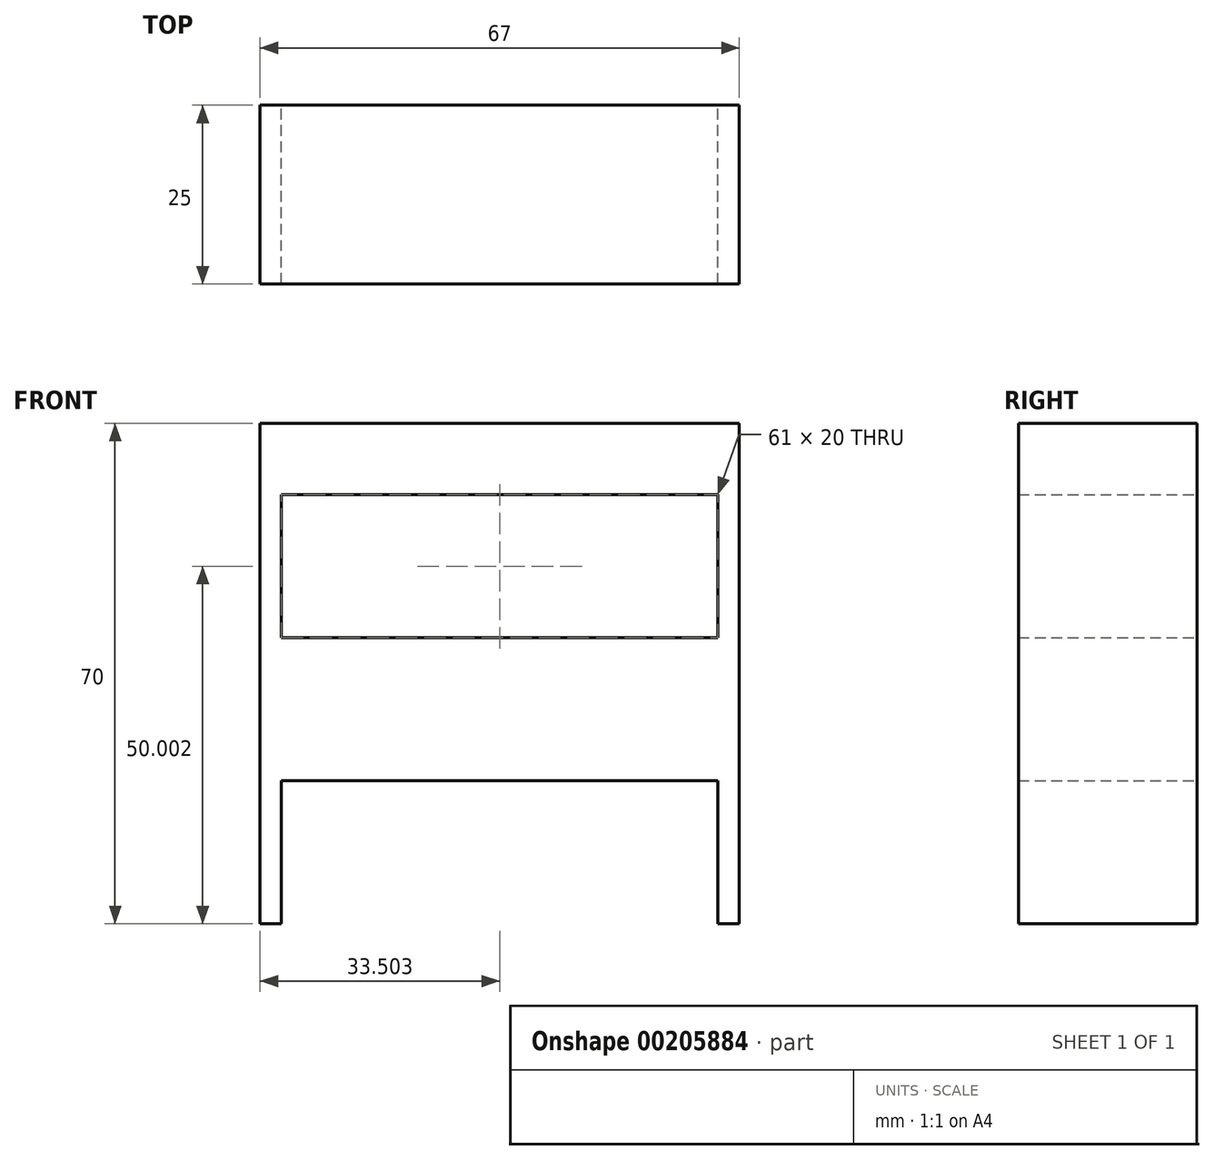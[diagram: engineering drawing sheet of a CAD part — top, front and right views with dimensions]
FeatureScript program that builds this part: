
annotation { "Feature Type Name" : "Feature", "Feature Type Description" : "" }
export const myFeature = defineFeature(function(context is Context, id is Id, definition is map)
    precondition{}
    {
        {
            var Q0;
            Q0=qCreatedBy(makeId("Front.planeOp"),FACE);
            var sketch = newSketch(context, id + "F0", { "sketchPlane" : qUnion([Q0])});
            skLineSegment(sketch, "E0.top", {"start": v(-11.27, 0.1) * mm, "end": v(-14.27, 0.1) * mm});
            skLineSegment(sketch, "E0.left", {"start": v(-11.27, 40.1) * mm, "end": v(-11.27, 20.1) * mm});
            skLineSegment(sketch, "E1.bottom", {"start": v(52.73, 70.1) * mm, "end": v(49.73, 70.1) * mm});
            skLineSegment(sketch, "E1.top", {"start": v(52.73, 0.1) * mm, "end": v(49.73, 0.1) * mm});
            skLineSegment(sketch, "E1.left", {"start": v(52.73, 70.1) * mm, "end": v(52.73, 0.1) * mm});
            skLineSegment(sketch, "E1.right", {"start": v(49.73, 40.1) * mm, "end": v(49.73, 20.1) * mm});
            skLineSegment(sketch, "E2.bottom", {"start": v(49.73, 40.1) * mm, "end": v(-11.27, 40.1) * mm});
            skLineSegment(sketch, "E2.top", {"start": v(49.73, 60.1) * mm, "end": v(-11.27, 60.1) * mm});
            skLineSegment(sketch, "E3.bottom", {"start": v(49.73, 70.1) * mm, "end": v(-14.27, 70.1) * mm});
            skLineSegment(sketch, "E3.top", {"start": v(49.73, 20.1) * mm, "end": v(-11.27, 20.1) * mm});
            skLineSegment(sketch, "E4.trimOffspring", {"start": v(49.73, 60.1) * mm, "end": v(49.73, 0.1) * mm});
            skLineSegment(sketch, "E5.trimOffspring", {"start": v(-11.27, 60.1) * mm, "end": v(-11.27, 0.1) * mm});
            skLineSegment(sketch, "E6", {"start": v(-14.27, 70.1) * mm, "end": v(-14.27, 0.1) * mm});
            skSolve(sketch);
        }
        {
            var Q0;
            Q0 = qSketchRegion(id + "F0", true);
            extrude(context, id + "F1", {"entities" : qUnion([Q0]), "depth" : 25 * mm});
        }
    });
